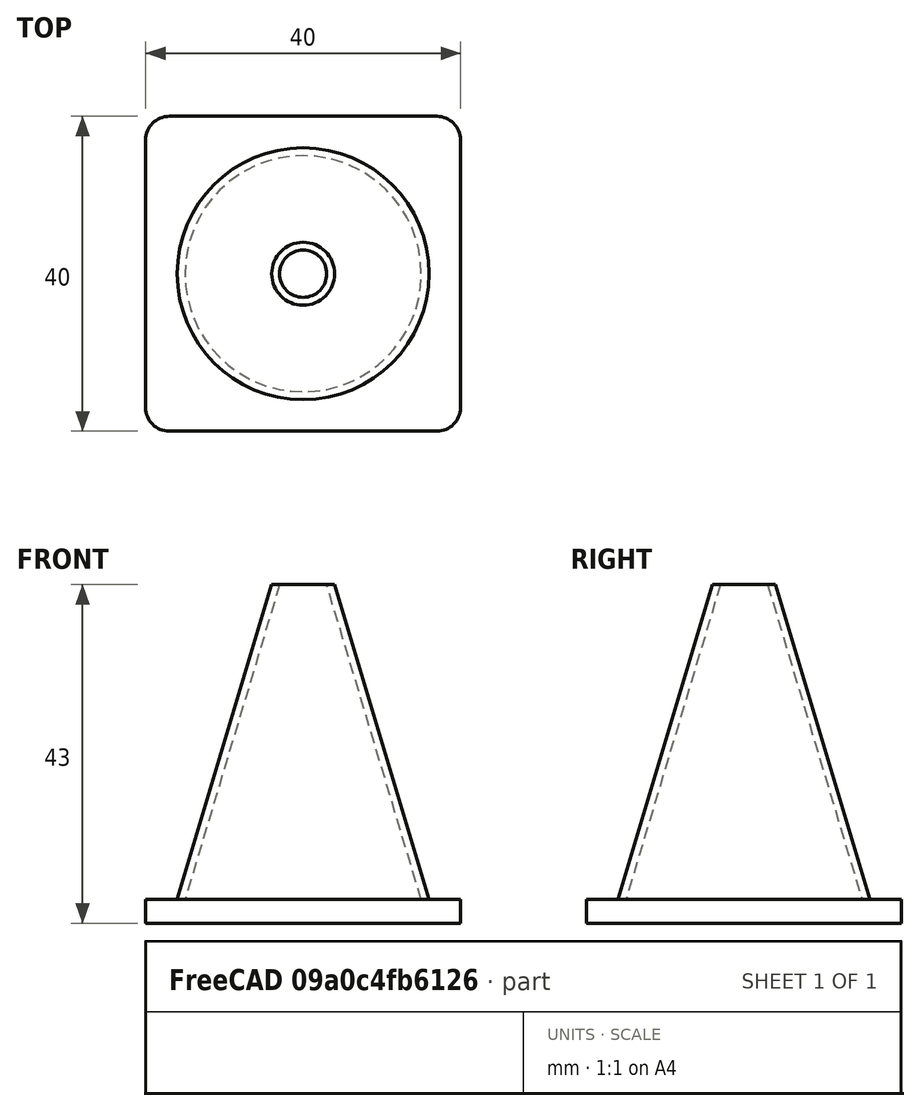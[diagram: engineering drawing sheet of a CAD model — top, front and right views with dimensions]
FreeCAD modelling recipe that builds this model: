
FCSTD DOCUMENT  (FreeCAD 0.21R33771 (Git))
Label: OJT1_T14R02_con_trafic
License: All rights reserved
LicenseURL: http://en.wikipedia.org/wiki/All_rights_reserved
objects: Part::Cone×2, Part::Box×1, Part::Fillet×1, Part::Cut×1, Part::MultiFuse×1
note: 6 computed .brp shape members not serialized (recipe doc carries the construction recipe); baked Part::Feature solids carry a one-line shape summary decoded from their .brp

FEATURE [Part::Box] Box  label="Cube"
  AttacherType = Attacher::AttachEngine3D
  Height = 3
  Length = 40
  Width = 40
FEATURE [Part::Fillet] Fillet
  Base = -> Box
  Edges = 4 edges r=3: [Edge1,Edge3,Edge5,Edge7]
FEATURE [Part::Cone] Cone
  Angle = 360
  AttacherType = Attacher::AttachEngine3D
  Height = 40
  Placement = pos=(20,20,3) rot=(0,0,1;0rad)
  Radius1 = 16
  Radius2 = 4
FEATURE [Part::Cone] Cone001
  Angle = 360
  AttacherType = Attacher::AttachEngine3D
  Height = 40
  Placement = pos=(20,20,3) rot=(0,0,1;0rad)
  Radius1 = 15
  Radius2 = 3
FEATURE [Part::Cut] Cut
  Base = -> Cone
  Refine = true
  Tool = -> Cone001
FEATURE [Part::MultiFuse] Fusion  label="con_trafic"
  Refine = true
  Shapes = -> [Fillet,Cut]
